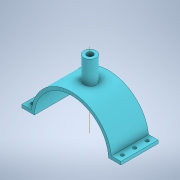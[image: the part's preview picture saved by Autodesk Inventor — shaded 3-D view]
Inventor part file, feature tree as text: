
AUTODESK INVENTOR PART (.ipt)
format: ipt  version: 2021 (Build 250183000, 183)  size: 166,912 bytes
history: native  units: in
note: dims shown in document units (in); Inventor stores cm internally (conversion verified against a paired STEP export)
features: sketch x4, extrude x3, hole x1, mirror x1, plane x1
ambient origin geometry x8: Origin, YZ Plane, XZ Plane, XY Plane, X Axis, Y Axis, Z Axis, Center Point
bodies: Body1 (feature_tree)
feature tree (10):
  extrude  "Extrusion5"  Depth=0.25in
  hole  "Hole3"  [1 undecoded]
  mirror  "Mirror3"
  plane  "Work Plane7"
  extrude  "Extrusion11"  Depth=0.25in TaperAngle=0.0deg
  extrude  "Extrusion13"  Depth=1.0in
  sketch  "Sketch8"  dims[d52=6.0in d53=0.25in]
  sketch  "Sketch9"  dims[d54=0.75in d55=0.125in]
  sketch  "Sketch20"  dims[d56=0.25in d57=3.0in d58=0.0in]
  sketch  "Sketch22"  dims[d59=0.5in d60=1.1811in d62=1.0in d63=0.3937in d65=1.0in d67=0.266in d68=0.75in d69=0.438in d70=0.25in d71=0.5635in d72=1.0in d73=0.8108in d100=3.125in d101=1.0in d102=2.0in d103=0.0in d111=0.5in d112=1.0in d113=0.0in d11=1.0in d12=1.0in d13=1.0in d14=0.15in d15=0.25in d16=0.375in d17=0.5635in d18=0.75in d19=0.8108in d20=0.0625in d21=0.75in d22=0.375in]
note: 1 required parameter value undecoded (feature->parameter linkage not recoverable at this tier; creation-order binding heuristic only, values carry confidence <= 0.55)
